FCSTD DOCUMENT  (FreeCAD 0.18R16161 (Git))
Label: Supports
License: All rights reserved
LicenseURL: http://en.wikipedia.org/wiki/All_rights_reserved
objects: Sketcher::SketchObject×1, PartDesign::Body×1
note: 2 computed .brp shape members not serialized (recipe doc carries the construction recipe); baked Part::Feature solids carry a one-line shape summary decoded from their .brp

FEATURE [Sketcher::SketchObject] Sketch
  MapMode = 5
  Support = -> [XY_Plane]
  sketch-geometry (20):
    g0: LineSegment StartX=-9.98313 StartY=9.98788 StartZ=0 EndX=129.991 EndY=9.98788 EndZ=0
    g1: LineSegment StartX=129.991 StartY=9.98788 StartZ=0 EndX=129.991 EndY=0.00714 EndZ=0
    g2: LineSegment StartX=129.991 StartY=0.00714 StartZ=0 EndX=-9.98313 EndY=0.00714 EndZ=0
    g3: LineSegment StartX=-9.98313 StartY=0.00714 StartZ=0 EndX=-9.98313 EndY=9.98788 EndZ=0
    g4: LineSegment StartX=0 StartY=0 StartZ=0 EndX=10.002 EndY=0 EndZ=0
    g5: LineSegment StartX=10.002 StartY=0 StartZ=0 EndX=10.002 EndY=-69.9909 EndZ=0
    g6: LineSegment StartX=10.002 StartY=-69.9909 StartZ=0 EndX=0 EndY=-69.9909 EndZ=0
    g7: LineSegment StartX=0 StartY=-69.9909 StartZ=0 EndX=0 EndY=0 EndZ=0
    g8: LineSegment StartX=129.991 StartY=0.00714 StartZ=0 EndX=120.014 EndY=0.00714 EndZ=0
    g9: LineSegment StartX=120.014 StartY=0.00714 StartZ=0 EndX=120.014 EndY=-50.0052 EndZ=0
    g10: LineSegment StartX=120.014 StartY=-50.0052 StartZ=0 EndX=129.991 EndY=-50.0052 EndZ=0
    g11: LineSegment StartX=129.991 StartY=-50.0052 StartZ=0 EndX=129.991 EndY=0.00714 EndZ=0
    g12: LineSegment StartX=-9.98313 StartY=9.98788 StartZ=0 EndX=0 EndY=9.98788 EndZ=0
    g13: LineSegment StartX=0 StartY=9.98788 StartZ=0 EndX=0 EndY=22.019 EndZ=0
    g14: LineSegment StartX=0 StartY=22.019 StartZ=0 EndX=-9.98313 EndY=22.019 EndZ=0
    g15: LineSegment StartX=-9.98313 StartY=22.019 StartZ=0 EndX=-9.98313 EndY=9.98788 EndZ=0
    g16: LineSegment StartX=-9.98313 StartY=22.019 StartZ=0 EndX=70.0161 EndY=22.019 EndZ=0
    g17: LineSegment StartX=70.0161 StartY=22.019 StartZ=0 EndX=70.0161 EndY=31.9741 EndZ=0
    g18: LineSegment StartX=70.0161 StartY=31.9741 StartZ=0 EndX=-9.98313 EndY=31.9741 EndZ=0
    g19: LineSegment StartX=-9.98313 StartY=31.9741 StartZ=0 EndX=-9.98313 EndY=22.019 EndZ=0
  constraints (44):
    c: Coincident(g0,g1)
    c: Coincident(g1,g2)
    c: Coincident(g2,g3)
    c: Coincident(g3,g0)
    c: Horizontal(g0)
    c: Horizontal(g2)
    c: Vertical(g1)
    c: Vertical(g3)
    c: Coincident(g4,g5)
    c: Coincident(g5,g6)
    c: Coincident(g6,g7)
    c: Coincident(g7,g4)
    c: Horizontal(g4)
    c: Horizontal(g6)
    c: Vertical(g5)
    c: Vertical(g7)
    c: Coincident(g8,g9)
    c: Coincident(g9,g10)
    c: Coincident(g10,g11)
    c: Coincident(g11,g8)
    c: Horizontal(g8)
    c: Horizontal(g10)
    c: Vertical(g9)
    c: Vertical(g11)
    c: Coincident(g8,g1)
    c: Coincident(g12,g13)
    c: Coincident(g13,g14)
    c: Coincident(g14,g15)
    c: Coincident(g15,g12)
    c: Horizontal(g12)
    c: Horizontal(g14)
    c: Vertical(g13)
    c: Vertical(g15)
    c: Coincident(g12,g0)
    c: PointOnObject(g13,g-2)
    c: Coincident(g16,g17)
    c: Coincident(g17,g18)
    c: Coincident(g18,g19)
    c: Coincident(g19,g16)
    c: Horizontal(g16)
    c: Horizontal(g18)
    c: Vertical(g17)
    c: Vertical(g19)
    c: Coincident(g16,g14)
FEATURE [PartDesign::Body] Body
  Group = -> [Sketch]
  Origin = -> Origin
